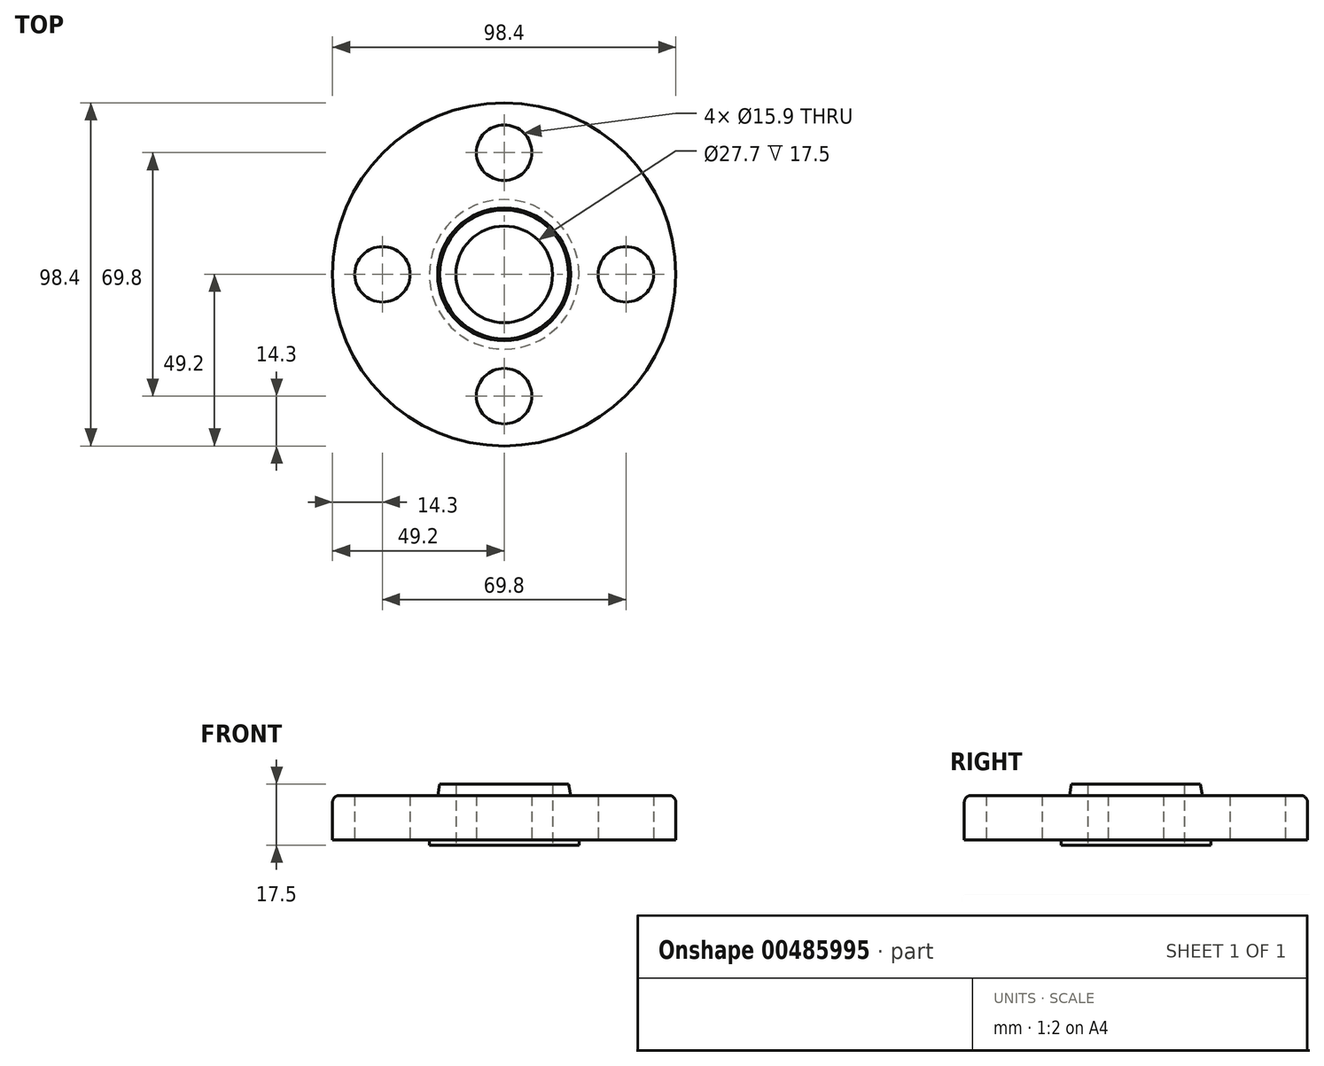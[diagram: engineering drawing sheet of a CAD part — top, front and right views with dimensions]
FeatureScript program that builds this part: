
annotation { "Feature Type Name" : "Feature", "Feature Type Description" : "" }
export const myFeature = defineFeature(function(context is Context, id is Id, definition is map)
    precondition{}
    {
        {
            var Q0;
            Q0=qCreatedBy(makeId("Front.planeOp"),FACE);
            var sketch = newSketch(context, id + "F0", { "sketchPlane" : qUnion([Q0])});
            skLineSegment(sketch, "E0", {"start": v(0, 0) * mm, "end": v(-21.45, 0) * mm});
            skLineSegment(sketch, "E1", {"start": v(-21.45, 0) * mm, "end": v(-21.45, 1.6) * mm});
            skLineSegment(sketch, "E2", {"start": v(-21.45, 1.6) * mm, "end": v(-49.2, 1.6) * mm});
            skLineSegment(sketch, "E3", {"start": v(-49.2, 1.6) * mm, "end": v(-49.2, 12.3) * mm});
            skLineSegment(sketch, "E4", {"start": v(0, 17.5) * mm, "end": v(0, 0) * mm});
            skLineSegment(sketch, "E5", {"start": v(-47.2, 14.3) * mm, "end": v(-19.05, 14.3) * mm});
            skLineSegment(sketch, "E6", {"start": v(-19.05, 14.3) * mm, "end": v(-18.49, 17.5) * mm});
            skLineSegment(sketch, "E7", {"start": v(-18.49, 17.5) * mm, "end": v(0, 17.5) * mm});
            skPoint(sketch, "E8.visualSharp", {"position": v(-49.2, 14.3) * mm});
            skArc(sketch, "E8.filletArc", {"start": v(-47.2, 14.3) * mm, "mid": v(-48.61, 13.71) * mm, "end": v(-49.2, 12.3) * mm});
            skSolve(sketch);
        }
        {
            var Q0;
            Q0=makeQuery(id+"F0.imprint","IMPRINT",FACE,{"disambiguationData":[TD([[makeQuery(id+"F0.imprint","IMPRINT",EDGE,{"derivedFrom":sQuery(id+"F0.wireOp",EDGE,"E0")}),-1.0]])]});
            var Q1;
            Q1=sQuery(id+"F0.wireOp",EDGE,"E4");
            revolve(context, id + "F1", {"entities" : qUnion([Q0]), "axis" : qUnion([Q1]), "revolveType" : RevolveType.FULL});
        }
        {
            var Q0;
            Q0=makeQuery(id+"F1.opRevolve","SWEPT_FACE",FACE,{"disambiguationData":[OSD([sQuery(id+"F0.wireOp",EDGE,"E0")])]});
            var sketch = newSketch(context, id + "F2", { "sketchPlane" : qUnion([Q0])});
            skCircle(sketch, "E9", {"center": v(0, 0) * mm, "radius": 13.85 * mm});
            skSolve(sketch);
        }
        {
            var Q0;
            Q0 = qSketchRegion(id + "F2", true);
            extrude(context, id + "F3", {"entities" : qUnion([Q0]), "operationType" : NewBodyOperationType.REMOVE, "endBound" : BoundingType.THROUGH_ALL, "oppositeDirection" : true, "depth" : 25 * mm});
        }
        {
            var Q0;
            Q0=makeQuery(id+"F1.opRevolve","SWEPT_FACE",FACE,{"disambiguationData":[OSD([sQuery(id+"F0.wireOp",EDGE,"E2")])]});
            var sketch = newSketch(context, id + "F4", { "sketchPlane" : qUnion([Q0])});
            skCircle(sketch, "E10", {"center": v(0, 34.9) * mm, "radius": 7.95 * mm});
            skCircle(sketch, "E11.1.0", {"center": v(-34.9, 0) * mm, "radius": 7.95 * mm});
            skCircle(sketch, "E11.2.0", {"center": v(0, -34.9) * mm, "radius": 7.95 * mm});
            skPoint(sketch, "E11.center", {"position": v(0, 0) * mm});
            skCircle(sketch, "E12.1.3.0", {"center": v(34.9, 0) * mm, "radius": 7.95 * mm});
            skSolve(sketch);
        }
        {
            var Q0;
            Q0 = qSketchRegion(id + "F4", true);
            extrude(context, id + "F5", {"entities" : qUnion([Q0]), "operationType" : NewBodyOperationType.REMOVE, "endBound" : BoundingType.THROUGH_ALL, "oppositeDirection" : true, "depth" : 25 * mm});
        }
    });
